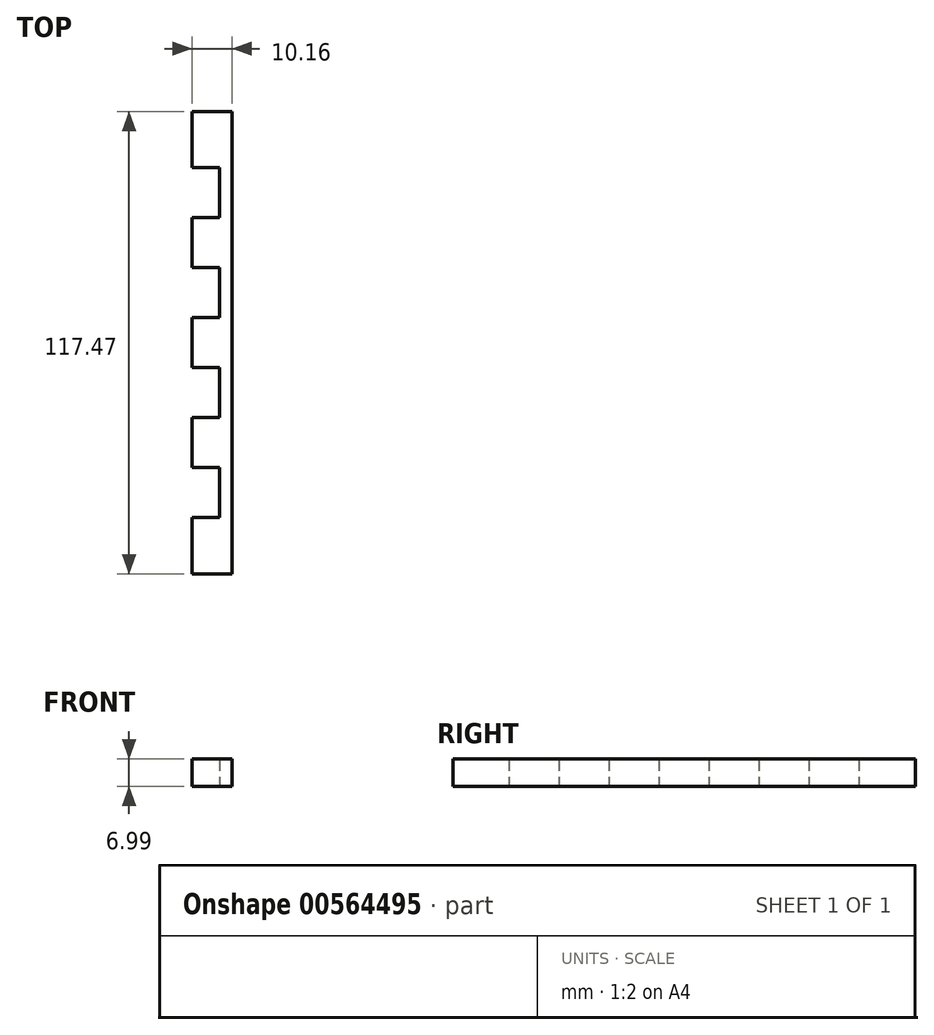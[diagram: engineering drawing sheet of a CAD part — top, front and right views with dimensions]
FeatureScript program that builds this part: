
annotation { "Feature Type Name" : "Feature", "Feature Type Description" : "" }
export const myFeature = defineFeature(function(context is Context, id is Id, definition is map)
    precondition{}
    {
        {
            var Q0;
            Q0=qCreatedBy(makeId("Top.planeOp"),FACE);
            var sketch = newSketch(context, id + "F0", { "sketchPlane" : qUnion([Q0])});
            skLineSegment(sketch, "E0.bottom", {"start": v(0, 0) * mm, "end": v(10.16, 0) * mm});
            skLineSegment(sketch, "E0.top", {"start": v(0, -117.48) * mm, "end": v(10.16, -117.48) * mm});
            skLineSegment(sketch, "E0.left", {"start": v(0, 0) * mm, "end": v(0, -14.29) * mm});
            skLineSegment(sketch, "E0.right", {"start": v(10.16, 0) * mm, "end": v(10.16, -117.48) * mm});
            skLineSegment(sketch, "E1", {"start": v(0, -14.29) * mm, "end": v(6.99, -14.29) * mm});
            skLineSegment(sketch, "E2", {"start": v(6.99, -14.29) * mm, "end": v(6.99, -26.99) * mm});
            skLineSegment(sketch, "E3", {"start": v(6.99, -26.99) * mm, "end": v(0, -26.99) * mm});
            skLineSegment(sketch, "E4", {"start": v(0, -26.99) * mm, "end": v(0, -39.69) * mm});
            skLineSegment(sketch, "E5", {"start": v(0, -39.69) * mm, "end": v(6.99, -39.69) * mm});
            skLineSegment(sketch, "E6", {"start": v(6.99, -39.69) * mm, "end": v(6.99, -52.39) * mm});
            skLineSegment(sketch, "E7", {"start": v(6.99, -52.39) * mm, "end": v(0, -52.39) * mm});
            skLineSegment(sketch, "E8", {"start": v(0, -52.39) * mm, "end": v(0, -65.09) * mm});
            skLineSegment(sketch, "E9", {"start": v(0, -65.09) * mm, "end": v(6.99, -65.09) * mm});
            skLineSegment(sketch, "E10", {"start": v(6.99, -65.09) * mm, "end": v(6.99, -77.79) * mm});
            skLineSegment(sketch, "E11", {"start": v(6.99, -77.79) * mm, "end": v(0, -77.79) * mm});
            skLineSegment(sketch, "E12.trimOffspring", {"start": v(0, -77.79) * mm, "end": v(0, -90.49) * mm});
            skLineSegment(sketch, "E13", {"start": v(0, -90.49) * mm, "end": v(6.99, -90.49) * mm});
            skLineSegment(sketch, "E14", {"start": v(6.99, -90.49) * mm, "end": v(6.99, -103.19) * mm});
            skLineSegment(sketch, "E15", {"start": v(6.99, -103.19) * mm, "end": v(0, -103.19) * mm});
            skLineSegment(sketch, "E16.trimOffspring", {"start": v(0, -103.19) * mm, "end": v(0, -117.48) * mm});
            skSolve(sketch);
        }
        {
            var Q0;
            Q0=makeQuery(id+"F0.imprint","IMPRINT",FACE,{"disambiguationData":[TD([[makeQuery(id+"F0.imprint","IMPRINT",EDGE,{"derivedFrom":sQuery(id+"F0.wireOp",EDGE,"E0.bottom")}),-1.0]])]});
            extrude(context, id + "F1", {"entities" : qUnion([Q0]), "depth" : 7 * mm, "offsetDistance" : 25.4 * mm});
        }
    });
